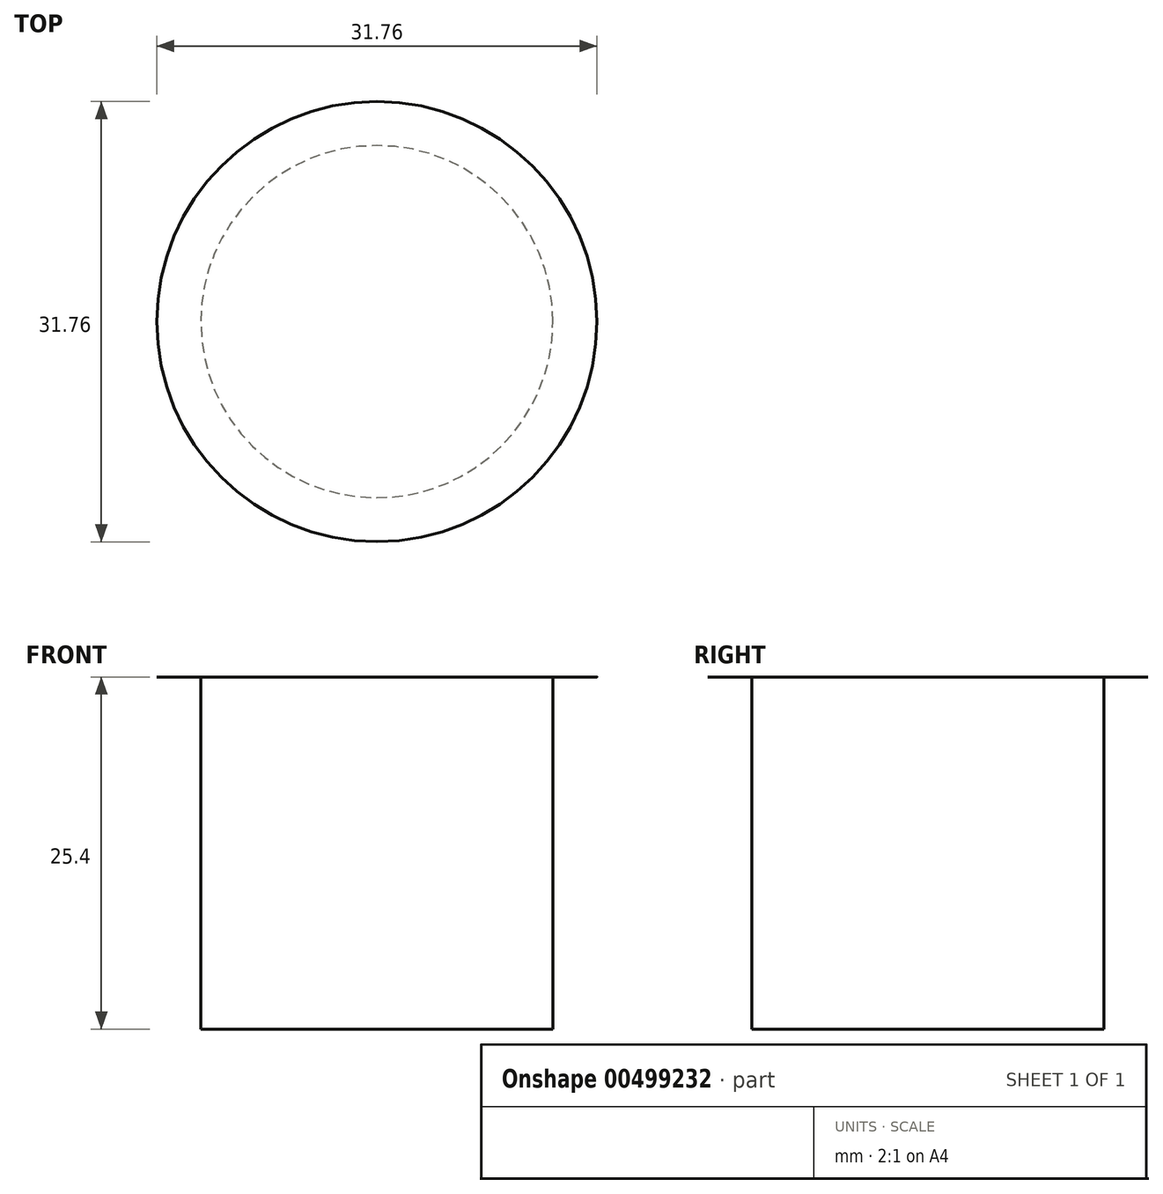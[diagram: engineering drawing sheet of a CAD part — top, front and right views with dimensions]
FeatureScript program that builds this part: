
annotation { "Feature Type Name" : "Feature", "Feature Type Description" : "" }
export const myFeature = defineFeature(function(context is Context, id is Id, definition is map)
    precondition{}
    {
        {
            var Q0;
            Q0=qCreatedBy(makeId("Top.planeOp"),FACE);
            var sketch = newSketch(context, id + "F0", { "sketchPlane" : qUnion([Q0])});
            skCircle(sketch, "E0", {"center": v(0, 0) * mm, "radius": 15.88 * mm});
            skSolve(sketch);
        }
        {
            var Q0;
            Q0=qSketchRegion(id+"F0",true);
            extrude(context, id + "F1", {"entities" : qUnion([Q0]), "depth" : 1 / 406.4 * mm, "offsetDistance" : 25.4 * mm});
        }
        {
            var Q0;
            Q0=makeQuery(id+"F1.opExtrude","CAP_FACE",FACE,{"disambiguationData":[OSD([sQuery(id+"F0.wireOp",EDGE,"E0")])],"isStart":true});
            var sketch = newSketch(context, id + "F2", { "sketchPlane" : qUnion([Q0])});
            skCircle(sketch, "E1", {"center": v(0, 0) * mm, "radius": 12.7 * mm});
            skSolve(sketch);
        }
        {
            var Q0;
            Q0=qSketchRegion(id+"F2",true);
            extrude(context, id + "F3", {"entities" : qUnion([Q0]), "operationType" : NewBodyOperationType.ADD, "depth" : 25.4 * mm, "offsetDistance" : 25.4 * mm});
        }
    });
